# Revit family: NBS_DudleyIndustries_PprTwlDpnsrs_BehindTheMirrorRange_PaperTowelDispenser
name_source: partatom
category: Specialty Equipment
revit_build: Autodesk Revit 2016 (Build: 20150220_1215(x64)
units: mm (PartAtom-declared; Revit-internal decimal feet)

## family parameters
Cut with Voids When Loaded = No
Host = Face
OmniClass Number = 23.40.20.21.17
OmniClass Title = Paper Towel Dispensers, Disposal Units
Part Type = Normal
Room Calculation Point = No
Round Connector Dimension = Use Diameter
Shared = No

## types (1)
- BehindTheMirrorRangePaperTowelDispenser
    AssetType = Fixed
    BIMObjectName = NBS_DudleyIndustries_PaperTowelDispensers_BehindtheMirrorRange_PaperTowelDispenser
    Category = Pr_40_70_22_62:Paper towel dispensers
    Color = Stainless steel
    Default Elevation = 1200 mm
    Description = Behing the mirror paper towel dispenser
    DispenserCabinetMaterial = NBS_Concept
    DurationUnit = year
    ExpectedLife = 5
    Features = Brushed Stainless Steel flat bottomed ‘behind the mirror’ paper towel dispenser, loaded through spring-loaded flaps at the base, uses C fold multi-fold interleaved hand towels
    Finish = Brushed
    Form = Wall mounted
    Grade = EN1.4509
    IfcExportAs = IfcFurnitureType
    IfcExportType = NOTDEFINED
    MainColor = Stainless steel
    ManufacturerName = Dudley Industries
    ManufacturerURL = www.dudleyindustries.com/
    Material = Stainless steel
    MaterialsBody = Stainless steel
    MaterialsFinishColour = Brushed
    ModelNumber = 92294
    ModelReference = Behind the Mirror Range: Paper Towel Dispenser
    NBSCertification = www.nationalbimlibrary.com/cert/s31ln2n3
    NBSDescription = Paper towel dispensers
    NBSReference = 45-35-72/344
    Name = PaperTowelDispensers_BehindTheMirrorRange_PaperTowelDispenser_DudleyIndustries
    NominalDepth = 120 mm  [stored 0.393701 ft]
    NominalHeight = 491 mm  [stored 1.61089 ft]
    NominalLength = 270 mm  [stored 0.885827 ft]
    NominalWidth = 270 mm  [stored 0.885827 ft]
    Operation = Manual
    ProductInformation = www.dudleyindustries.com/wp-content/uploads/2016/11/Flat-End-Paper-Towel-Dispenser.pdf
    Size = 270 x 485 x 120 mm
    Style = Paper Towel Dispenser
    TowelsTowelType = C fold or muti-fold interleaved
    TowelsWidth = 260 mm max
    Uniclass2015Code = Pr_40_70_22_62
    Uniclass2015Title = Paper towel dispensers
    Uniclass2015Version = Products v1.7
    Version = 2
    WarrantyDescription = 1 year warranty
    WarrantyDurationParts = 1
    WarrantyDurationUnit = year

note: [stored X ft] marks values corroborated as IEEE doubles in the binary element streams (Revit-internal decimal feet)

## geometry (parser evidence)
native form markers: Sweep x2
no freeform markers — native parametric forms only
